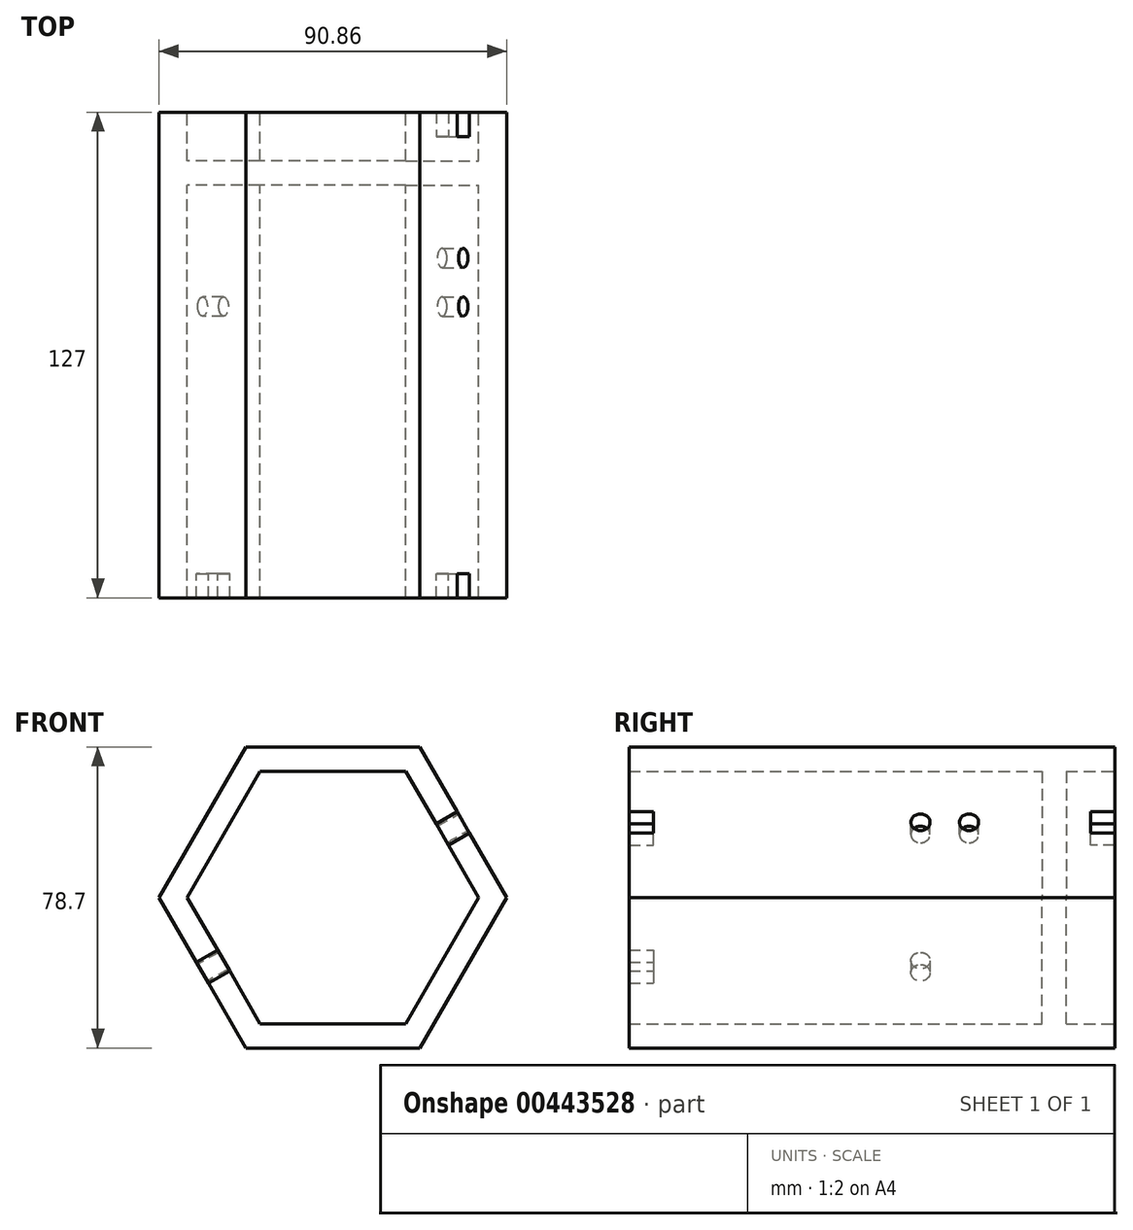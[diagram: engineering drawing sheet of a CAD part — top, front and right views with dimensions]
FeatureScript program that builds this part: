
annotation { "Feature Type Name" : "Feature", "Feature Type Description" : "" }
export const myFeature = defineFeature(function(context is Context, id is Id, definition is map)
    precondition{}
    {
        {
            var Q0;
            Q0=qCreatedBy(makeId("Front.planeOp"),FACE);
            var sketch = newSketch(context, id + "F0", { "sketchPlane" : qUnion([Q0])});
            skLineSegment(sketch, "E0.1", {"start": v(19.05, -33) * mm, "end": v(-19.05, -33) * mm});
            skLineSegment(sketch, "E0.2", {"start": v(-19.05, -33) * mm, "end": v(-38.1, 0) * mm});
            skLineSegment(sketch, "E0.3", {"start": v(-38.1, 0) * mm, "end": v(-19.05, 33) * mm});
            skLineSegment(sketch, "E0.4", {"start": v(-19.05, 33) * mm, "end": v(19.05, 33) * mm});
            skLineSegment(sketch, "E0.5", {"start": v(19.05, 33) * mm, "end": v(38.1, 0) * mm});
            skLineSegment(sketch, "E1", {"start": v(19.05, -33) * mm, "end": v(38.1, 0) * mm});
            skLineSegment(sketch, "E2.1", {"start": v(22.72, 39.35) * mm, "end": v(45.43, 0) * mm});
            skLineSegment(sketch, "E2.2", {"start": v(45.43, 0) * mm, "end": v(22.72, -39.35) * mm});
            skLineSegment(sketch, "E2.3", {"start": v(22.72, -39.35) * mm, "end": v(-22.72, -39.35) * mm});
            skLineSegment(sketch, "E2.4", {"start": v(-22.72, -39.35) * mm, "end": v(-45.43, 0) * mm});
            skLineSegment(sketch, "E2.5", {"start": v(-45.43, 0) * mm, "end": v(-22.72, 39.35) * mm});
            skLineSegment(sketch, "E3", {"start": v(22.72, 39.35) * mm, "end": v(-22.72, 39.35) * mm});
            skSolve(sketch);
        }
        {
            var Q0;
            Q0 = qSketchRegion(id + "F0", true);
            extrude(context, id + "F1", {"entities" : qUnion([Q0]), "depth" : 114.3 * mm});
        }
        {
            var Q0;
            Q0 = qSketchRegion(id + "F0", true);
            extrude(context, id + "F2", {"entities" : qUnion([Q0]), "operationType" : NewBodyOperationType.ADD, "oppositeDirection" : true, "depth" : 12.7 * mm});
        }
        {
            var Q0;
            Q0=qCreatedBy(makeId("Front.planeOp"),FACE);
            var sketch = newSketch(context, id + "F3", { "sketchPlane" : qUnion([Q0])});
            skLineSegment(sketch, "E4.0", {"start": v(38.1, 0) * mm, "end": v(19.05, -33) * mm});
            skLineSegment(sketch, "E4.1", {"start": v(19.05, -33) * mm, "end": v(-19.05, -33) * mm});
            skLineSegment(sketch, "E4.2", {"start": v(-19.05, -33) * mm, "end": v(-38.1, 0) * mm});
            skLineSegment(sketch, "E4.3", {"start": v(-38.1, 0) * mm, "end": v(-19.05, 33) * mm});
            skLineSegment(sketch, "E4.4", {"start": v(-19.05, 33) * mm, "end": v(19.05, 33) * mm});
            skLineSegment(sketch, "E4.5", {"start": v(19.05, 33) * mm, "end": v(38.1, 0) * mm});
            skSolve(sketch);
        }
        {
            var Q0;
            Q0 = qSketchRegion(id + "F3", true);
            extrude(context, id + "F4", {"entities" : qUnion([Q0]), "operationType" : NewBodyOperationType.ADD, "depth" : 6.35 * mm});
        }
        {
            var Q0;
            {var subQ0=sQuery(id+"F0.wireOp",EDGE,"E2.1");Q0=makeQuery(id+"F2.boolean.opBoolean","MERGE",FACE,{"derivedFrom":[makeQuery(id+"F1.opExtrude","SWEPT_FACE",FACE,{"disambiguationData":[OSD([subQ0])]}),makeQuery(id+"F2.opExtrude","SWEPT_FACE",FACE,{"disambiguationData":[OSD([subQ0])]})]});}
            var sketch = newSketch(context, id + "F5", { "sketchPlane" : qUnion([Q0])});
            skLineSegment(sketch, "E5.bottom", {"start": v(-114.3, -3.18) * mm, "end": v(-107.95, -3.18) * mm});
            skLineSegment(sketch, "E5.top", {"start": v(-114.3, 3.17) * mm, "end": v(-107.95, 3.17) * mm});
            skLineSegment(sketch, "E5.left", {"start": v(-114.3, -3.18) * mm, "end": v(-114.3, 3.18) * mm});
            skLineSegment(sketch, "E5.right", {"start": v(-107.95, -3.18) * mm, "end": v(-107.95, 3.18) * mm});
            skPoint(sketch, "E6", {"position": v(-114.3, 0) * mm});
            skSolve(sketch);
        }
        {
            var Q0;
            Q0 = qSketchRegion(id + "F5", true);
            extrude(context, id + "F6", {"entities" : qUnion([Q0]), "operationType" : NewBodyOperationType.REMOVE, "oppositeDirection" : true, "depth" : 6.35 * mm});
        }
        {
            var Q0;
            {var subQ0=sQuery(id+"F0.wireOp",EDGE,"E2.4");Q0=makeQuery(id+"F2.boolean.opBoolean","MERGE",FACE,{"derivedFrom":[makeQuery(id+"F1.opExtrude","SWEPT_FACE",FACE,{"disambiguationData":[OSD([subQ0])]}),makeQuery(id+"F2.opExtrude","SWEPT_FACE",FACE,{"disambiguationData":[OSD([subQ0])]})]});}
            var sketch = newSketch(context, id + "F7", { "sketchPlane" : qUnion([Q0])});
            skLineSegment(sketch, "E7.bottom", {"start": v(114.3, 3.18) * mm, "end": v(107.95, 3.18) * mm});
            skLineSegment(sketch, "E7.top", {"start": v(114.3, -3.18) * mm, "end": v(107.95, -3.18) * mm});
            skLineSegment(sketch, "E7.left", {"start": v(114.3, 3.17) * mm, "end": v(114.3, -3.17) * mm});
            skLineSegment(sketch, "E7.right", {"start": v(107.95, 3.17) * mm, "end": v(107.95, -3.17) * mm});
            skPoint(sketch, "E8", {"position": v(114.3, 0) * mm});
            skSolve(sketch);
        }
        {
            var Q0;
            Q0 = qSketchRegion(id + "F7", true);
            extrude(context, id + "F8", {"entities" : qUnion([Q0]), "operationType" : NewBodyOperationType.REMOVE, "oppositeDirection" : true, "depth" : 6.35 * mm});
        }
        {
            var Q0;
            {var subQ0=sQuery(id+"F0.wireOp",EDGE,"E2.4");Q0=makeQuery(id+"F2.boolean.opBoolean","MERGE",FACE,{"derivedFrom":[makeQuery(id+"F1.opExtrude","SWEPT_FACE",FACE,{"disambiguationData":[OSD([subQ0])]}),makeQuery(id+"F2.opExtrude","SWEPT_FACE",FACE,{"disambiguationData":[OSD([subQ0])]})]});}
            var sketch = newSketch(context, id + "F9", { "sketchPlane" : qUnion([Q0])});
            skCircle(sketch, "E9", {"center": v(38.1, 0) * mm, "radius": 2.5 * mm});
            skSolve(sketch);
        }
        {
            var Q0;
            Q0 = qSketchRegion(id + "F9", true);
            extrude(context, id + "F10", {"entities" : qUnion([Q0]), "operationType" : NewBodyOperationType.REMOVE, "oppositeDirection" : true, "depth" : 6.35 * mm});
        }
        {
            var Q0;
            {var subQ0=sQuery(id+"F0.wireOp",EDGE,"E2.1");Q0=makeQuery(id+"F2.boolean.opBoolean","MERGE",FACE,{"derivedFrom":[makeQuery(id+"F1.opExtrude","SWEPT_FACE",FACE,{"disambiguationData":[OSD([subQ0])]}),makeQuery(id+"F2.opExtrude","SWEPT_FACE",FACE,{"disambiguationData":[OSD([subQ0])]})]});}
            var sketch = newSketch(context, id + "F11", { "sketchPlane" : qUnion([Q0])});
            skCircle(sketch, "E10", {"center": v(-38.1, 0) * mm, "radius": 2.5 * mm});
            skCircle(sketch, "E11", {"center": v(-25.4, 0) * mm, "radius": 2.5 * mm});
            skSolve(sketch);
        }
        {
            var Q0;
            Q0 = qSketchRegion(id + "F11", true);
            extrude(context, id + "F12", {"entities" : qUnion([Q0]), "operationType" : NewBodyOperationType.REMOVE, "oppositeDirection" : true, "depth" : 6.35 * mm});
        }
        {
            var Q0;
            {var subQ0=sQuery(id+"F0.wireOp",EDGE,"E2.1");Q0=makeQuery(id+"F2.boolean.opBoolean","MERGE",FACE,{"derivedFrom":[makeQuery(id+"F1.opExtrude","SWEPT_FACE",FACE,{"disambiguationData":[OSD([subQ0])]}),makeQuery(id+"F2.opExtrude","SWEPT_FACE",FACE,{"disambiguationData":[OSD([subQ0])]})]});}
            var sketch = newSketch(context, id + "F13", { "sketchPlane" : qUnion([Q0])});
            skLineSegment(sketch, "E12.bottom", {"start": v(12.7, -3.17) * mm, "end": v(6.35, -3.17) * mm});
            skLineSegment(sketch, "E12.top", {"start": v(12.7, 3.18) * mm, "end": v(6.35, 3.18) * mm});
            skLineSegment(sketch, "E12.left", {"start": v(12.7, -3.18) * mm, "end": v(12.7, 3.17) * mm});
            skLineSegment(sketch, "E12.right", {"start": v(6.35, -3.17) * mm, "end": v(6.35, 3.17) * mm});
            skPoint(sketch, "E13", {"position": v(12.7, 0) * mm});
            skSolve(sketch);
        }
        {
            var Q0;
            Q0 = qSketchRegion(id + "F13", true);
            extrude(context, id + "F14", {"entities" : qUnion([Q0]), "operationType" : NewBodyOperationType.REMOVE, "oppositeDirection" : true, "depth" : 6.35 * mm});
        }
    });
